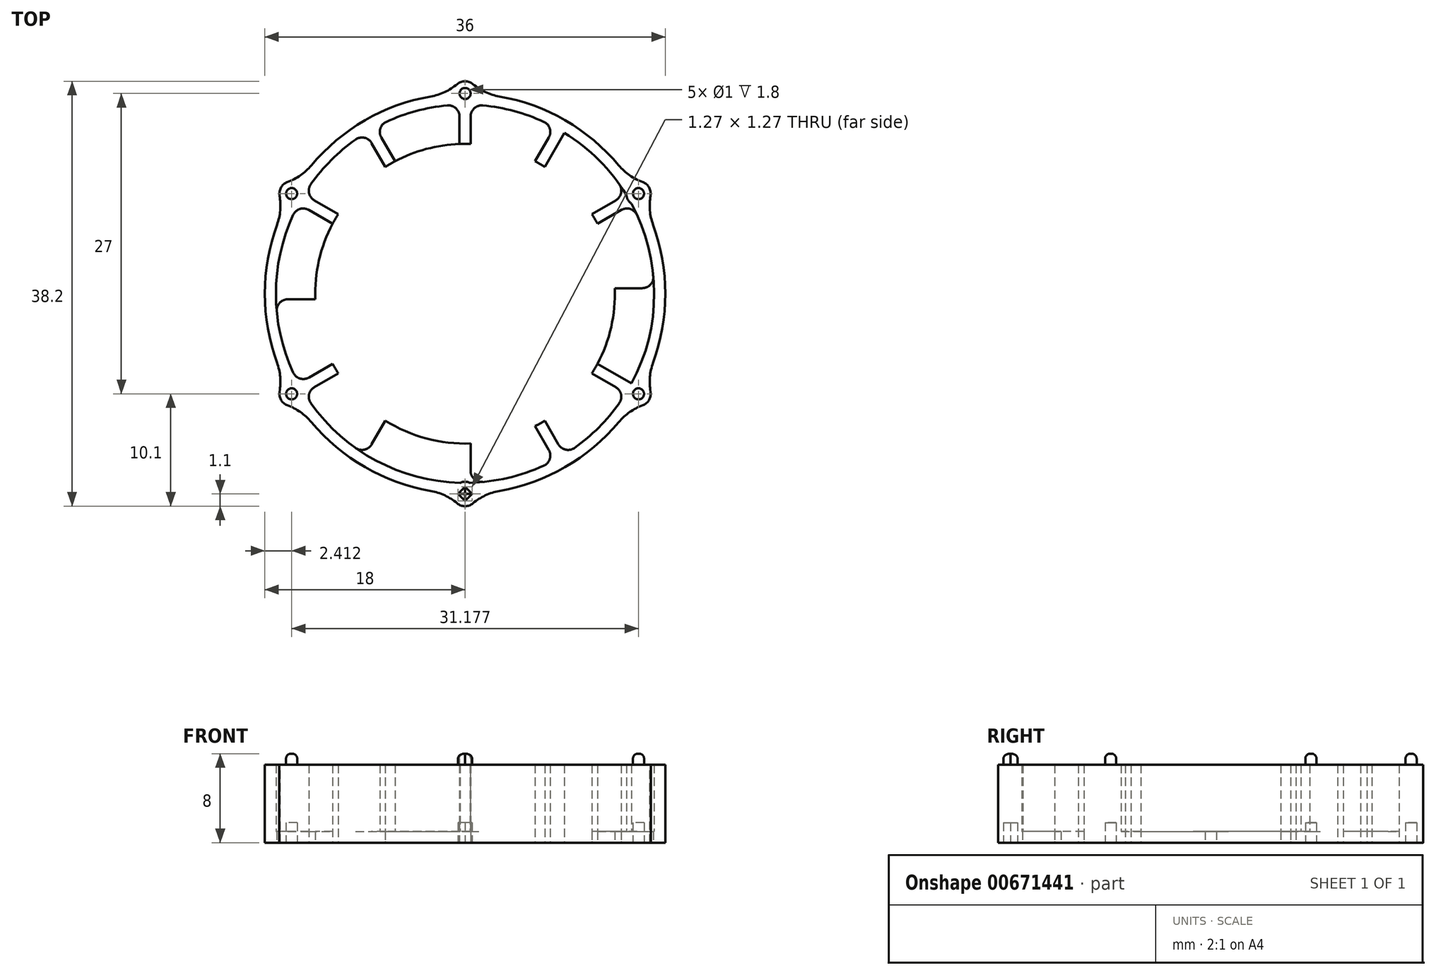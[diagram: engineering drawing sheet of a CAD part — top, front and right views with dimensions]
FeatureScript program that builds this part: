
annotation { "Feature Type Name" : "Feature", "Feature Type Description" : "" }
export const myFeature = defineFeature(function(context is Context, id is Id, definition is map)
    precondition{}
    {
        {
            var Q0;
            Q0=qCreatedBy(makeId("Top.planeOp"),FACE);
            var sketch = newSketch(context, id + "F0", { "sketchPlane" : qUnion([Q0])});
            skCircle(sketch, "E0", {"center": v(0, 0) * mm, "radius": 18 * mm});
            skCircle(sketch, "E1.0", {"center": v(0, 0) * mm, "radius": 17 * mm});
            skLineSegment(sketch, "E2.bottom", {"start": v(8.56, 15.83) * mm, "end": v(9.43, 15.33) * mm});
            skLineSegment(sketch, "E2.top", {"start": v(-9.43, -15.33) * mm, "end": v(-8.56, -15.83) * mm});
            skLineSegment(sketch, "E2.left", {"start": v(8.56, 15.83) * mm, "end": v(-9.43, -15.33) * mm});
            skLineSegment(sketch, "E2.right", {"start": v(9.43, 15.33) * mm, "end": v(-8.56, -15.83) * mm});
            skLineSegment(sketch, "E3.bottom", {"start": v(15.33, 9.43) * mm, "end": v(15.83, 8.56) * mm});
            skLineSegment(sketch, "E3.top", {"start": v(-15.83, -8.56) * mm, "end": v(-15.33, -9.43) * mm});
            skLineSegment(sketch, "E3.left", {"start": v(15.33, 9.43) * mm, "end": v(-15.83, -8.56) * mm});
            skLineSegment(sketch, "E3.right", {"start": v(15.83, 8.56) * mm, "end": v(-15.33, -9.43) * mm});
            skLineSegment(sketch, "E4", {"start": v(-38.35, 0) * mm, "end": v(39.17, 0) * mm, "construction": true});
            skLineSegment(sketch, "E5", {"start": v(0, 42.5) * mm, "end": v(0, -42.47) * mm, "construction": true});
            skLineSegment(sketch, "E6.bottom", {"start": v(-18, 0.5) * mm, "end": v(18, 0.5) * mm});
            skLineSegment(sketch, "E6.top", {"start": v(-18, -0.5) * mm, "end": v(18, -0.5) * mm});
            skLineSegment(sketch, "E6.left", {"start": v(-18, 0.5) * mm, "end": v(-18, -0.5) * mm});
            skLineSegment(sketch, "E6.right", {"start": v(18, 0.5) * mm, "end": v(18, -0.5) * mm});
            skLineSegment(sketch, "E7.bottom", {"start": v(-15.33, 9.43) * mm, "end": v(15.83, -8.56) * mm});
            skLineSegment(sketch, "E7.top", {"start": v(-15.83, 8.56) * mm, "end": v(15.33, -9.43) * mm});
            skLineSegment(sketch, "E7.left", {"start": v(-15.33, 9.43) * mm, "end": v(-15.83, 8.56) * mm});
            skLineSegment(sketch, "E7.right", {"start": v(15.83, -8.56) * mm, "end": v(15.33, -9.43) * mm});
            skLineSegment(sketch, "E8.bottom", {"start": v(-0.5, 18) * mm, "end": v(0.5, 18) * mm});
            skLineSegment(sketch, "E8.top", {"start": v(-0.5, -18) * mm, "end": v(0.5, -18) * mm});
            skLineSegment(sketch, "E8.left", {"start": v(-0.5, 18) * mm, "end": v(-0.5, -18) * mm});
            skLineSegment(sketch, "E8.right", {"start": v(0.5, 18) * mm, "end": v(0.5, -18) * mm});
            skLineSegment(sketch, "E9.bottom", {"start": v(-9.43, 15.33) * mm, "end": v(-8.56, 15.83) * mm});
            skLineSegment(sketch, "E9.top", {"start": v(8.56, -15.83) * mm, "end": v(9.43, -15.33) * mm});
            skLineSegment(sketch, "E9.left", {"start": v(-9.43, 15.33) * mm, "end": v(8.56, -15.83) * mm});
            skLineSegment(sketch, "E9.right", {"start": v(-8.56, 15.83) * mm, "end": v(9.43, -15.33) * mm});
            skCircle(sketch, "E10", {"center": v(0, 0) * mm, "radius": 13.47 * mm});
            skSolve(sketch);
        }
        {
            var Q0;
            Q0=qCreatedBy(makeId("Top.planeOp"),FACE);
            var sketch = newSketch(context, id + "F1", { "sketchPlane" : qUnion([Q0])});
            skCircle(sketch, "E11", {"center": v(0, 0) * mm, "radius": 18 * mm});
            skCircle(sketch, "E12", {"center": v(0, 0) * mm, "radius": 17 * mm});
            skSolve(sketch);
        }
        {
            var Q0;
            Q0=makeQuery(id+"F1.imprint","IMPRINT",FACE,{"disambiguationData":[TD([[makeQuery(id+"F1.imprint","IMPRINT",EDGE,{"derivedFrom":sQuery(id+"F1.wireOp",EDGE,"E11")}),1.0]])]});
            extrude(context, id + "F2", {"entities" : qUnion([Q0]), "depth" : 7 * mm, "offsetDistance" : 25 * mm});
        }
        {
            var Q0;
            {var subQ0=sQuery(id+"F0.wireOp",EDGE,"E7.bottom");var subQ1=sQuery(id+"F0.wireOp",EDGE,"E1.0");var subQ2=makeQuery(id+"F0.imprint","INTERSECT",VERTEX,{"disambiguationData":[OD(0.0)],"derivedFrom":[subQ1,subQ0]});Q0=makeQuery(id+"F0.imprint","IMPRINT",FACE,{"disambiguationData":[TD([[makeQuery(id+"F0.imprint","IMPRINT",EDGE,{"disambiguationData":[TD([[subQ2,-1.0]])],"derivedFrom":subQ1}),1.0]])]});}
            var Q1;
            {var subQ0=sQuery(id+"F0.wireOp",EDGE,"E2.right");var subQ1=sQuery(id+"F0.wireOp",EDGE,"E1.0");var subQ2=makeQuery(id+"F0.imprint","INTERSECT",VERTEX,{"disambiguationData":[OD(0.0)],"derivedFrom":[subQ1,subQ0]});Q1=makeQuery(id+"F0.imprint","IMPRINT",FACE,{"disambiguationData":[TD([[makeQuery(id+"F0.imprint","IMPRINT",EDGE,{"disambiguationData":[TD([[subQ2,-1.0]])],"derivedFrom":subQ1}),1.0]])]});}
            var Q2;
            {var subQ0=sQuery(id+"F0.wireOp",EDGE,"E3.left");var subQ1=sQuery(id+"F0.wireOp",EDGE,"E1.0");var subQ2=makeQuery(id+"F0.imprint","INTERSECT",VERTEX,{"disambiguationData":[OD(1.0)],"derivedFrom":[subQ1,subQ0]});Q2=makeQuery(id+"F0.imprint","IMPRINT",FACE,{"disambiguationData":[TD([[makeQuery(id+"F0.imprint","IMPRINT",EDGE,{"disambiguationData":[TD([[subQ2,-1.0]])],"derivedFrom":subQ1}),1.0]])]});}
            var Q3;
            {var subQ0=sQuery(id+"F0.wireOp",EDGE,"E9.right");var subQ1=sQuery(id+"F0.wireOp",EDGE,"E1.0");var subQ2=makeQuery(id+"F0.imprint","INTERSECT",VERTEX,{"disambiguationData":[OD(0.0)],"derivedFrom":[subQ1,subQ0]});Q3=makeQuery(id+"F0.imprint","IMPRINT",FACE,{"disambiguationData":[TD([[makeQuery(id+"F0.imprint","IMPRINT",EDGE,{"disambiguationData":[TD([[subQ2,-1.0]])],"derivedFrom":subQ1}),1.0]])]});}
            var Q4;
            {var subQ0=sQuery(id+"F0.wireOp",EDGE,"E8.right");var subQ1=sQuery(id+"F0.wireOp",EDGE,"E1.0");var subQ2=makeQuery(id+"F0.imprint","INTERSECT",VERTEX,{"disambiguationData":[OD(0.0)],"derivedFrom":[subQ1,subQ0]});Q4=makeQuery(id+"F0.imprint","IMPRINT",FACE,{"disambiguationData":[TD([[makeQuery(id+"F0.imprint","IMPRINT",EDGE,{"disambiguationData":[TD([[subQ2,-1.0]])],"derivedFrom":subQ1}),1.0]])]});}
            var Q5;
            {var subQ0=sQuery(id+"F0.wireOp",EDGE,"E7.top");var subQ1=sQuery(id+"F0.wireOp",EDGE,"E1.0");var subQ2=makeQuery(id+"F0.imprint","INTERSECT",VERTEX,{"disambiguationData":[OD(1.0)],"derivedFrom":[subQ1,subQ0]});Q5=makeQuery(id+"F0.imprint","IMPRINT",FACE,{"disambiguationData":[TD([[makeQuery(id+"F0.imprint","IMPRINT",EDGE,{"disambiguationData":[TD([[subQ2,-1.0]])],"derivedFrom":subQ1}),1.0]])]});}
            var Q6;
            {var subQ0=sQuery(id+"F0.wireOp",EDGE,"E9.left");var subQ1=sQuery(id+"F0.wireOp",EDGE,"E1.0");var subQ2=makeQuery(id+"F0.imprint","INTERSECT",VERTEX,{"disambiguationData":[OD(1.0)],"derivedFrom":[subQ1,subQ0]});Q6=makeQuery(id+"F0.imprint","IMPRINT",FACE,{"disambiguationData":[TD([[makeQuery(id+"F0.imprint","IMPRINT",EDGE,{"disambiguationData":[TD([[subQ2,-1.0]])],"derivedFrom":subQ1}),1.0]])]});}
            extrude(context, id + "F3", {"entities" : qUnion([Q0, Q1, Q2, Q3, Q4, Q5, Q6]), "operationType" : NewBodyOperationType.ADD, "depth" : 7 * mm, "offsetDistance" : 25 * mm});
        }
        {
            var Q0;
            Q0=makeQuery(id+"F1.imprint","IMPRINT",FACE,{"disambiguationData":[TD([[makeQuery(id+"F1.imprint","IMPRINT",EDGE,{"derivedFrom":sQuery(id+"F1.wireOp",EDGE,"E11")}),1.0]])]});
            var Q1;
            Q1=makeQuery(id+"F1.imprint","IMPRINT",FACE,{"disambiguationData":[TD([[makeQuery(id+"F1.imprint","IMPRINT",EDGE,{"derivedFrom":sQuery(id+"F1.wireOp",EDGE,"E12")}),1.0]])]});
            extrude(context, id + "F4", {"entities" : qUnion([Q0, Q1]), "operationType" : NewBodyOperationType.ADD, "depth" : 1 * mm, "offsetDistance" : 25 * mm});
        }
        {
            var Q0;
            Q0=qCreatedBy(makeId("Top.planeOp"),FACE);
            var sketch = newSketch(context, id + "F5", { "sketchPlane" : qUnion([Q0])});
            skCircle(sketch, "E13", {"center": v(0, 0) * mm, "radius": 18 * mm});
            skLineSegment(sketch, "E14", {"start": v(0, 18) * mm, "end": v(0, -18) * mm, "construction": true});
            skLineSegment(sketch, "E15", {"start": v(15.59, 9) * mm, "end": v(0, 0) * mm, "construction": true});
            skLineSegment(sketch, "E16", {"start": v(9, 15.59) * mm, "end": v(0, 0) * mm, "construction": true});
            skLineSegment(sketch, "E17", {"start": v(0, 0) * mm, "end": v(18, 0) * mm, "construction": true});
            skLineSegment(sketch, "E18", {"start": v(0, 0) * mm, "end": v(15.59, -9) * mm, "construction": true});
            skLineSegment(sketch, "E19", {"start": v(0, 0) * mm, "end": v(9, -15.59) * mm, "construction": true});
            skLineSegment(sketch, "E20", {"start": v(0, 0) * mm, "end": v(-9, 15.59) * mm, "construction": true});
            skLineSegment(sketch, "E21", {"start": v(0, 0) * mm, "end": v(-15.59, 9) * mm, "construction": true});
            skLineSegment(sketch, "E22", {"start": v(0, 0) * mm, "end": v(-18, 0) * mm, "construction": true});
            skLineSegment(sketch, "E23", {"start": v(0, 0) * mm, "end": v(-15.59, -9) * mm, "construction": true});
            skLineSegment(sketch, "E24", {"start": v(0, 0) * mm, "end": v(-9, -15.59) * mm, "construction": true});
            skCircle(sketch, "E25", {"center": v(0, 18) * mm, "radius": 1.1 * mm});
            skCircle(sketch, "E26", {"center": v(15.59, 9) * mm, "radius": 1.1 * mm});
            skCircle(sketch, "E27", {"center": v(15.59, -9) * mm, "radius": 1.1 * mm});
            skCircle(sketch, "E28", {"center": v(0, -18) * mm, "radius": 1.1 * mm});
            skCircle(sketch, "E29", {"center": v(-15.59, -9) * mm, "radius": 1.1 * mm});
            skCircle(sketch, "E30", {"center": v(-15.59, 9) * mm, "radius": 1.1 * mm});
            skCircle(sketch, "E31", {"center": v(-15.59, 9) * mm, "radius": 0.5 * mm});
            skCircle(sketch, "E32", {"center": v(0, 18) * mm, "radius": 0.5 * mm});
            skCircle(sketch, "E33", {"center": v(15.59, 9) * mm, "radius": 0.5 * mm});
            skCircle(sketch, "E34", {"center": v(15.59, -9) * mm, "radius": 0.5 * mm});
            skCircle(sketch, "E35", {"center": v(-15.59, -9) * mm, "radius": 0.5 * mm});
            skLineSegment(sketch, "E36.bottom", {"start": v(0.64, -18) * mm, "end": v(0, -18.64) * mm});
            skLineSegment(sketch, "E36.top", {"start": v(0, -17.36) * mm, "end": v(-0.64, -18) * mm});
            skLineSegment(sketch, "E36.left", {"start": v(0.64, -18) * mm, "end": v(0, -17.36) * mm});
            skLineSegment(sketch, "E36.right", {"start": v(0, -18.64) * mm, "end": v(-0.64, -18) * mm});
            skSolve(sketch);
        }
        {
            var Q0;
            {var subQ0=sQuery(id+"F5.wireOp",EDGE,"E30");var subQ1=sQuery(id+"F5.wireOp",EDGE,"E13");var subQ2=makeQuery(id+"F5.imprint","INTERSECT",VERTEX,{"disambiguationData":[OD(0.0)],"derivedFrom":[subQ1,subQ0]});Q0=makeQuery(id+"F5.imprint","IMPRINT",FACE,{"disambiguationData":[TD([[makeQuery(id+"F5.imprint","IMPRINT",EDGE,{"disambiguationData":[TD([[subQ2,-1.0]])],"derivedFrom":subQ1}),1.0]])]});}
            var Q1;
            {var subQ0=sQuery(id+"F5.wireOp",EDGE,"E30");var subQ1=sQuery(id+"F5.wireOp",EDGE,"E13");var subQ2=makeQuery(id+"F5.imprint","INTERSECT",VERTEX,{"disambiguationData":[OD(0.0)],"derivedFrom":[subQ1,subQ0]});Q1=makeQuery(id+"F5.imprint","IMPRINT",FACE,{"disambiguationData":[TD([[makeQuery(id+"F5.imprint","IMPRINT",EDGE,{"disambiguationData":[TD([[subQ2,-1.0]])],"derivedFrom":subQ1}),-1.0]])]});}
            var Q2;
            {var subQ0=sQuery(id+"F5.wireOp",EDGE,"E25");var subQ1=sQuery(id+"F5.wireOp",EDGE,"E13");var subQ2=makeQuery(id+"F5.imprint","INTERSECT",VERTEX,{"disambiguationData":[OD(0.0)],"derivedFrom":[subQ1,subQ0]});Q2=makeQuery(id+"F5.imprint","IMPRINT",FACE,{"disambiguationData":[TD([[makeQuery(id+"F5.imprint","IMPRINT",EDGE,{"disambiguationData":[TD([[subQ2,-1.0]])],"derivedFrom":subQ1}),1.0]])]});}
            var Q3;
            {var subQ0=sQuery(id+"F5.wireOp",EDGE,"E25");var subQ1=sQuery(id+"F5.wireOp",EDGE,"E13");var subQ2=makeQuery(id+"F5.imprint","INTERSECT",VERTEX,{"disambiguationData":[OD(0.0)],"derivedFrom":[subQ1,subQ0]});Q3=makeQuery(id+"F5.imprint","IMPRINT",FACE,{"disambiguationData":[TD([[makeQuery(id+"F5.imprint","IMPRINT",EDGE,{"disambiguationData":[TD([[subQ2,-1.0]])],"derivedFrom":subQ1}),-1.0]])]});}
            var Q4;
            {var subQ0=sQuery(id+"F5.wireOp",EDGE,"E26");var subQ1=sQuery(id+"F5.wireOp",EDGE,"E13");var subQ2=makeQuery(id+"F5.imprint","INTERSECT",VERTEX,{"disambiguationData":[OD(0.0)],"derivedFrom":[subQ1,subQ0]});Q4=makeQuery(id+"F5.imprint","IMPRINT",FACE,{"disambiguationData":[TD([[makeQuery(id+"F5.imprint","IMPRINT",EDGE,{"disambiguationData":[TD([[subQ2,-1.0]])],"derivedFrom":subQ1}),-1.0]])]});}
            var Q5;
            {var subQ0=sQuery(id+"F5.wireOp",EDGE,"E26");var subQ1=sQuery(id+"F5.wireOp",EDGE,"E13");var subQ2=makeQuery(id+"F5.imprint","INTERSECT",VERTEX,{"disambiguationData":[OD(0.0)],"derivedFrom":[subQ1,subQ0]});Q5=makeQuery(id+"F5.imprint","IMPRINT",FACE,{"disambiguationData":[TD([[makeQuery(id+"F5.imprint","IMPRINT",EDGE,{"disambiguationData":[TD([[subQ2,-1.0]])],"derivedFrom":subQ1}),1.0]])]});}
            var Q6;
            {var subQ0=sQuery(id+"F5.wireOp",EDGE,"E29");var subQ1=sQuery(id+"F5.wireOp",EDGE,"E13");var subQ2=makeQuery(id+"F5.imprint","INTERSECT",VERTEX,{"disambiguationData":[OD(0.0)],"derivedFrom":[subQ1,subQ0]});Q6=makeQuery(id+"F5.imprint","IMPRINT",FACE,{"disambiguationData":[TD([[makeQuery(id+"F5.imprint","IMPRINT",EDGE,{"disambiguationData":[TD([[subQ2,-1.0]])],"derivedFrom":subQ1}),1.0]])]});}
            var Q7;
            {var subQ0=sQuery(id+"F5.wireOp",EDGE,"E29");var subQ1=sQuery(id+"F5.wireOp",EDGE,"E13");var subQ2=makeQuery(id+"F5.imprint","INTERSECT",VERTEX,{"disambiguationData":[OD(0.0)],"derivedFrom":[subQ1,subQ0]});Q7=makeQuery(id+"F5.imprint","IMPRINT",FACE,{"disambiguationData":[TD([[makeQuery(id+"F5.imprint","IMPRINT",EDGE,{"disambiguationData":[TD([[subQ2,-1.0]])],"derivedFrom":subQ1}),-1.0]])]});}
            var Q8;
            {var subQ3=sQuery(id+"F5.wireOp",EDGE,"E13");var subQ5=sQuery(id+"F5.wireOp",EDGE,"E28");var subQ6=makeQuery(id+"F5.imprint","INTERSECT",VERTEX,{"disambiguationData":[OD(0.0)],"derivedFrom":[subQ3,subQ5]});Q8=makeQuery(id+"F5.imprint","IMPRINT",FACE,{"disambiguationData":[TD([[makeQuery(id+"F5.imprint","IMPRINT",EDGE,{"disambiguationData":[TD([[subQ6,-1.0]])],"derivedFrom":subQ3}),1.0]])]});}
            var Q9;
            {var subQ6=sQuery(id+"F5.wireOp",EDGE,"E36.bottom");Q9=makeQuery(id+"F5.imprint","IMPRINT",FACE,{"disambiguationData":[TD([[makeQuery(id+"F5.imprint","IMPRINT",EDGE,{"derivedFrom":subQ6}),1.0]])]});}
            var Q10;
            {var subQ0=sQuery(id+"F5.wireOp",EDGE,"E27");var subQ1=sQuery(id+"F5.wireOp",EDGE,"E13");var subQ2=makeQuery(id+"F5.imprint","INTERSECT",VERTEX,{"disambiguationData":[OD(0.0)],"derivedFrom":[subQ1,subQ0]});Q10=makeQuery(id+"F5.imprint","IMPRINT",FACE,{"disambiguationData":[TD([[makeQuery(id+"F5.imprint","IMPRINT",EDGE,{"disambiguationData":[TD([[subQ2,-1.0]])],"derivedFrom":subQ1}),-1.0]])]});}
            var Q11;
            {var subQ0=sQuery(id+"F5.wireOp",EDGE,"E27");var subQ1=sQuery(id+"F5.wireOp",EDGE,"E13");var subQ2=makeQuery(id+"F5.imprint","INTERSECT",VERTEX,{"disambiguationData":[OD(0.0)],"derivedFrom":[subQ1,subQ0]});Q11=makeQuery(id+"F5.imprint","IMPRINT",FACE,{"disambiguationData":[TD([[makeQuery(id+"F5.imprint","IMPRINT",EDGE,{"disambiguationData":[TD([[subQ2,-1.0]])],"derivedFrom":subQ1}),1.0]])]});}
            var Q12;
            {var subQ0=sQuery(id+"F5.wireOp",EDGE,"E31");var subQ1=sQuery(id+"F5.wireOp",EDGE,"E13");var subQ2=makeQuery(id+"F5.imprint","INTERSECT",VERTEX,{"disambiguationData":[OD(0.0)],"derivedFrom":[subQ1,subQ0]});Q12=makeQuery(id+"F5.imprint","IMPRINT",FACE,{"disambiguationData":[TD([[makeQuery(id+"F5.imprint","IMPRINT",EDGE,{"disambiguationData":[TD([[subQ2,-1.0]])],"derivedFrom":subQ1}),1.0]])]});}
            var Q13;
            {var subQ0=sQuery(id+"F5.wireOp",EDGE,"E31");var subQ1=sQuery(id+"F5.wireOp",EDGE,"E13");var subQ2=makeQuery(id+"F5.imprint","INTERSECT",VERTEX,{"disambiguationData":[OD(0.0)],"derivedFrom":[subQ1,subQ0]});Q13=makeQuery(id+"F5.imprint","IMPRINT",FACE,{"disambiguationData":[TD([[makeQuery(id+"F5.imprint","IMPRINT",EDGE,{"disambiguationData":[TD([[subQ2,-1.0]])],"derivedFrom":subQ1}),-1.0]])]});}
            var Q14;
            {var subQ0=sQuery(id+"F5.wireOp",EDGE,"E32");var subQ1=sQuery(id+"F5.wireOp",EDGE,"E13");var subQ2=makeQuery(id+"F5.imprint","INTERSECT",VERTEX,{"disambiguationData":[OD(0.0)],"derivedFrom":[subQ1,subQ0]});Q14=makeQuery(id+"F5.imprint","IMPRINT",FACE,{"disambiguationData":[TD([[makeQuery(id+"F5.imprint","IMPRINT",EDGE,{"disambiguationData":[TD([[subQ2,-1.0]])],"derivedFrom":subQ1}),-1.0]])]});}
            var Q15;
            {var subQ0=sQuery(id+"F5.wireOp",EDGE,"E32");var subQ1=sQuery(id+"F5.wireOp",EDGE,"E13");var subQ2=makeQuery(id+"F5.imprint","INTERSECT",VERTEX,{"disambiguationData":[OD(0.0)],"derivedFrom":[subQ1,subQ0]});Q15=makeQuery(id+"F5.imprint","IMPRINT",FACE,{"disambiguationData":[TD([[makeQuery(id+"F5.imprint","IMPRINT",EDGE,{"disambiguationData":[TD([[subQ2,-1.0]])],"derivedFrom":subQ1}),1.0]])]});}
            var Q16;
            {var subQ0=sQuery(id+"F5.wireOp",EDGE,"E33");var subQ1=sQuery(id+"F5.wireOp",EDGE,"E13");var subQ2=makeQuery(id+"F5.imprint","INTERSECT",VERTEX,{"disambiguationData":[OD(0.0)],"derivedFrom":[subQ1,subQ0]});Q16=makeQuery(id+"F5.imprint","IMPRINT",FACE,{"disambiguationData":[TD([[makeQuery(id+"F5.imprint","IMPRINT",EDGE,{"disambiguationData":[TD([[subQ2,-1.0]])],"derivedFrom":subQ1}),-1.0]])]});}
            var Q17;
            {var subQ0=sQuery(id+"F5.wireOp",EDGE,"E33");var subQ1=sQuery(id+"F5.wireOp",EDGE,"E13");var subQ2=makeQuery(id+"F5.imprint","INTERSECT",VERTEX,{"disambiguationData":[OD(0.0)],"derivedFrom":[subQ1,subQ0]});Q17=makeQuery(id+"F5.imprint","IMPRINT",FACE,{"disambiguationData":[TD([[makeQuery(id+"F5.imprint","IMPRINT",EDGE,{"disambiguationData":[TD([[subQ2,-1.0]])],"derivedFrom":subQ1}),1.0]])]});}
            var Q18;
            {var subQ0=sQuery(id+"F5.wireOp",EDGE,"E34");var subQ1=sQuery(id+"F5.wireOp",EDGE,"E13");var subQ2=makeQuery(id+"F5.imprint","INTERSECT",VERTEX,{"disambiguationData":[OD(0.0)],"derivedFrom":[subQ1,subQ0]});Q18=makeQuery(id+"F5.imprint","IMPRINT",FACE,{"disambiguationData":[TD([[makeQuery(id+"F5.imprint","IMPRINT",EDGE,{"disambiguationData":[TD([[subQ2,-1.0]])],"derivedFrom":subQ1}),-1.0]])]});}
            var Q19;
            {var subQ0=sQuery(id+"F5.wireOp",EDGE,"E34");var subQ1=sQuery(id+"F5.wireOp",EDGE,"E13");var subQ2=makeQuery(id+"F5.imprint","INTERSECT",VERTEX,{"disambiguationData":[OD(0.0)],"derivedFrom":[subQ1,subQ0]});Q19=makeQuery(id+"F5.imprint","IMPRINT",FACE,{"disambiguationData":[TD([[makeQuery(id+"F5.imprint","IMPRINT",EDGE,{"disambiguationData":[TD([[subQ2,-1.0]])],"derivedFrom":subQ1}),1.0]])]});}
            var Q20;
            {var subQ1=sQuery(id+"F5.wireOp",EDGE,"E36.bottom");Q20=makeQuery(id+"F5.imprint","IMPRINT",FACE,{"disambiguationData":[TD([[makeQuery(id+"F5.imprint","IMPRINT",EDGE,{"derivedFrom":subQ1}),-1.0]])]});}
            var Q21;
            {var subQ0=sQuery(id+"F5.wireOp",EDGE,"E35");var subQ1=sQuery(id+"F5.wireOp",EDGE,"E13");var subQ2=makeQuery(id+"F5.imprint","INTERSECT",VERTEX,{"disambiguationData":[OD(0.0)],"derivedFrom":[subQ1,subQ0]});Q21=makeQuery(id+"F5.imprint","IMPRINT",FACE,{"disambiguationData":[TD([[makeQuery(id+"F5.imprint","IMPRINT",EDGE,{"disambiguationData":[TD([[subQ2,-1.0]])],"derivedFrom":subQ1}),-1.0]])]});}
            var Q22;
            {var subQ0=sQuery(id+"F5.wireOp",EDGE,"E35");var subQ1=sQuery(id+"F5.wireOp",EDGE,"E13");var subQ2=makeQuery(id+"F5.imprint","INTERSECT",VERTEX,{"disambiguationData":[OD(0.0)],"derivedFrom":[subQ1,subQ0]});Q22=makeQuery(id+"F5.imprint","IMPRINT",FACE,{"disambiguationData":[TD([[makeQuery(id+"F5.imprint","IMPRINT",EDGE,{"disambiguationData":[TD([[subQ2,-1.0]])],"derivedFrom":subQ1}),1.0]])]});}
            var Q23;
            {var subQ0=sQuery(id+"F5.wireOp",EDGE,"E36.top");var subQ1=sQuery(id+"F5.wireOp",EDGE,"E13");var subQ2=makeQuery(id+"F5.imprint","INTERSECT",VERTEX,{"derivedFrom":[subQ1,subQ0]});Q23=makeQuery(id+"F5.imprint","IMPRINT",FACE,{"disambiguationData":[TD([[makeQuery(id+"F5.imprint","IMPRINT",EDGE,{"disambiguationData":[TD([[subQ2,-1.0]])],"derivedFrom":subQ1}),1.0]])]});}
            extrude(context, id + "F6", {"entities" : qUnion([Q0, Q1, Q2, Q3, Q4, Q5, Q6, Q7, Q8, Q9, Q10, Q11, Q12, Q13, Q14, Q15, Q16, Q17, Q18, Q19, Q20, Q21, Q22, Q23]), "operationType" : NewBodyOperationType.ADD, "depth" : 7 * mm, "offsetDistance" : 25 * mm});
        }
        {
            var Q0;
            {var subQ0=sQuery(id+"F0.wireOp",EDGE,"E8.right");var subQ1=sQuery(id+"F0.wireOp",EDGE,"E1.0");Q0=makeQuery(id+"F3.opExtrude","SWEPT_EDGE",EDGE,{"disambiguationData":[OSD([subQ1,subQ0]),TDD([makeQuery(id+"F0.imprint","INTERSECT",VERTEX,{"disambiguationData":[OD(1.0)],"derivedFrom":[subQ1,subQ0]})])]});}
            var Q1;
            {var subQ0=sQuery(id+"F0.wireOp",EDGE,"E2.left");var subQ1=sQuery(id+"F0.wireOp",EDGE,"E1.0");Q1=makeQuery(id+"F3.opExtrude","SWEPT_EDGE",EDGE,{"disambiguationData":[OSD([subQ1,subQ0]),TDD([makeQuery(id+"F0.imprint","INTERSECT",VERTEX,{"disambiguationData":[OD(1.0)],"derivedFrom":[subQ1,subQ0]})])]});}
            var Q2;
            {var subQ0=sQuery(id+"F0.wireOp",EDGE,"E3.left");var subQ1=sQuery(id+"F0.wireOp",EDGE,"E1.0");Q2=makeQuery(id+"F3.opExtrude","SWEPT_EDGE",EDGE,{"disambiguationData":[OSD([subQ1,subQ0]),TDD([makeQuery(id+"F0.imprint","INTERSECT",VERTEX,{"disambiguationData":[OD(1.0)],"derivedFrom":[subQ1,subQ0]})])]});}
            var Q3;
            {var subQ0=sQuery(id+"F0.wireOp",EDGE,"E6.bottom");var subQ1=sQuery(id+"F0.wireOp",EDGE,"E1.0");Q3=makeQuery(id+"F3.opExtrude","SWEPT_EDGE",EDGE,{"disambiguationData":[OSD([subQ1,subQ0]),TDD([makeQuery(id+"F0.imprint","INTERSECT",VERTEX,{"disambiguationData":[OD(1.0)],"derivedFrom":[subQ1,subQ0]})])]});}
            var Q4;
            {var subQ0=sQuery(id+"F0.wireOp",EDGE,"E9.right");var subQ1=sQuery(id+"F0.wireOp",EDGE,"E1.0");Q4=makeQuery(id+"F3.opExtrude","SWEPT_EDGE",EDGE,{"disambiguationData":[OSD([subQ1,subQ0]),TDD([makeQuery(id+"F0.imprint","INTERSECT",VERTEX,{"disambiguationData":[OD(1.0)],"derivedFrom":[subQ1,subQ0]})])]});}
            var Q5;
            {var subQ0=sQuery(id+"F0.wireOp",EDGE,"E7.bottom");var subQ1=sQuery(id+"F0.wireOp",EDGE,"E1.0");Q5=makeQuery(id+"F3.opExtrude","SWEPT_EDGE",EDGE,{"disambiguationData":[OSD([subQ1,subQ0]),TDD([makeQuery(id+"F0.imprint","INTERSECT",VERTEX,{"disambiguationData":[OD(1.0)],"derivedFrom":[subQ1,subQ0]})])]});}
            var Q6;
            {var subQ0=sQuery(id+"F0.wireOp",EDGE,"E8.left");var subQ1=sQuery(id+"F0.wireOp",EDGE,"E1.0");Q6=makeQuery(id+"F3.opExtrude","SWEPT_EDGE",EDGE,{"disambiguationData":[OSD([subQ1,subQ0]),TDD([makeQuery(id+"F0.imprint","INTERSECT",VERTEX,{"disambiguationData":[OD(0.0)],"derivedFrom":[subQ1,subQ0]})])]});}
            var Q7;
            {var subQ0=sQuery(id+"F0.wireOp",EDGE,"E2.left");var subQ1=sQuery(id+"F0.wireOp",EDGE,"E1.0");Q7=makeQuery(id+"F3.opExtrude","SWEPT_EDGE",EDGE,{"disambiguationData":[OSD([subQ1,subQ0]),TDD([makeQuery(id+"F0.imprint","INTERSECT",VERTEX,{"disambiguationData":[OD(0.0)],"derivedFrom":[subQ1,subQ0]})])]});}
            var Q8;
            {var subQ0=sQuery(id+"F0.wireOp",EDGE,"E3.left");var subQ1=sQuery(id+"F0.wireOp",EDGE,"E1.0");Q8=makeQuery(id+"F3.opExtrude","SWEPT_EDGE",EDGE,{"disambiguationData":[OSD([subQ1,subQ0]),TDD([makeQuery(id+"F0.imprint","INTERSECT",VERTEX,{"disambiguationData":[OD(0.0)],"derivedFrom":[subQ1,subQ0]})])]});}
            var Q9;
            {var subQ0=sQuery(id+"F0.wireOp",EDGE,"E6.top");var subQ1=sQuery(id+"F0.wireOp",EDGE,"E1.0");Q9=makeQuery(id+"F3.opExtrude","SWEPT_EDGE",EDGE,{"disambiguationData":[OSD([subQ1,subQ0]),TDD([makeQuery(id+"F0.imprint","INTERSECT",VERTEX,{"disambiguationData":[OD(1.0)],"derivedFrom":[subQ1,subQ0]})])]});}
            var Q10;
            {var subQ0=sQuery(id+"F0.wireOp",EDGE,"E7.top");var subQ1=sQuery(id+"F0.wireOp",EDGE,"E1.0");Q10=makeQuery(id+"F3.opExtrude","SWEPT_EDGE",EDGE,{"disambiguationData":[OSD([subQ1,subQ0]),TDD([makeQuery(id+"F0.imprint","INTERSECT",VERTEX,{"disambiguationData":[OD(0.0)],"derivedFrom":[subQ1,subQ0]})])]});}
            var Q11;
            {var subQ0=sQuery(id+"F0.wireOp",EDGE,"E6.top");var subQ1=sQuery(id+"F0.wireOp",EDGE,"E1.0");Q11=makeQuery(id+"F3.opExtrude","SWEPT_EDGE",EDGE,{"disambiguationData":[OSD([subQ1,subQ0]),TDD([makeQuery(id+"F0.imprint","INTERSECT",VERTEX,{"disambiguationData":[OD(0.0)],"derivedFrom":[subQ1,subQ0]})])]});}
            var Q12;
            {var subQ0=sQuery(id+"F0.wireOp",EDGE,"E9.left");var subQ1=sQuery(id+"F0.wireOp",EDGE,"E1.0");Q12=makeQuery(id+"F3.opExtrude","SWEPT_EDGE",EDGE,{"disambiguationData":[OSD([subQ1,subQ0]),TDD([makeQuery(id+"F0.imprint","INTERSECT",VERTEX,{"disambiguationData":[OD(0.0)],"derivedFrom":[subQ1,subQ0]})])]});}
            var Q13;
            {var subQ0=sQuery(id+"F0.wireOp",EDGE,"E8.right");var subQ1=sQuery(id+"F0.wireOp",EDGE,"E1.0");Q13=makeQuery(id+"F3.opExtrude","SWEPT_EDGE",EDGE,{"disambiguationData":[OSD([subQ1,subQ0]),TDD([makeQuery(id+"F0.imprint","INTERSECT",VERTEX,{"disambiguationData":[OD(0.0)],"derivedFrom":[subQ1,subQ0]})])]});}
            var Q14;
            {var subQ0=sQuery(id+"F0.wireOp",EDGE,"E7.bottom");var subQ1=sQuery(id+"F0.wireOp",EDGE,"E1.0");Q14=makeQuery(id+"F3.opExtrude","SWEPT_EDGE",EDGE,{"disambiguationData":[OSD([subQ1,subQ0]),TDD([makeQuery(id+"F0.imprint","INTERSECT",VERTEX,{"disambiguationData":[OD(0.0)],"derivedFrom":[subQ1,subQ0]})])]});}
            var Q15;
            {var subQ0=sQuery(id+"F0.wireOp",EDGE,"E9.right");var subQ1=sQuery(id+"F0.wireOp",EDGE,"E1.0");Q15=makeQuery(id+"F3.opExtrude","SWEPT_EDGE",EDGE,{"disambiguationData":[OSD([subQ1,subQ0]),TDD([makeQuery(id+"F0.imprint","INTERSECT",VERTEX,{"disambiguationData":[OD(0.0)],"derivedFrom":[subQ1,subQ0]})])]});}
            var Q16;
            {var subQ0=sQuery(id+"F0.wireOp",EDGE,"E3.right");var subQ1=sQuery(id+"F0.wireOp",EDGE,"E1.0");Q16=makeQuery(id+"F3.opExtrude","SWEPT_EDGE",EDGE,{"disambiguationData":[OSD([subQ1,subQ0]),TDD([makeQuery(id+"F0.imprint","INTERSECT",VERTEX,{"disambiguationData":[OD(1.0)],"derivedFrom":[subQ1,subQ0]})])]});}
            var Q17;
            {var subQ0=sQuery(id+"F0.wireOp",EDGE,"E2.right");var subQ1=sQuery(id+"F0.wireOp",EDGE,"E1.0");Q17=makeQuery(id+"F3.opExtrude","SWEPT_EDGE",EDGE,{"disambiguationData":[OSD([subQ1,subQ0]),TDD([makeQuery(id+"F0.imprint","INTERSECT",VERTEX,{"disambiguationData":[OD(1.0)],"derivedFrom":[subQ1,subQ0]})])]});}
            var Q18;
            {var subQ0=sQuery(id+"F0.wireOp",EDGE,"E3.right");var subQ1=sQuery(id+"F0.wireOp",EDGE,"E1.0");Q18=makeQuery(id+"F3.opExtrude","SWEPT_EDGE",EDGE,{"disambiguationData":[OSD([subQ1,subQ0]),TDD([makeQuery(id+"F0.imprint","INTERSECT",VERTEX,{"disambiguationData":[OD(0.0)],"derivedFrom":[subQ1,subQ0]})])]});}
            var Q19;
            {var subQ0=sQuery(id+"F0.wireOp",EDGE,"E2.right");var subQ1=sQuery(id+"F0.wireOp",EDGE,"E1.0");Q19=makeQuery(id+"F3.opExtrude","SWEPT_EDGE",EDGE,{"disambiguationData":[OSD([subQ1,subQ0]),TDD([makeQuery(id+"F0.imprint","INTERSECT",VERTEX,{"disambiguationData":[OD(0.0)],"derivedFrom":[subQ1,subQ0]})])]});}
            var Q20;
            {var subQ0=sQuery(id+"F0.wireOp",EDGE,"E8.left");var subQ1=sQuery(id+"F0.wireOp",EDGE,"E1.0");Q20=makeQuery(id+"F3.opExtrude","SWEPT_EDGE",EDGE,{"disambiguationData":[OSD([subQ1,subQ0]),TDD([makeQuery(id+"F0.imprint","INTERSECT",VERTEX,{"disambiguationData":[OD(1.0)],"derivedFrom":[subQ1,subQ0]})])]});}
            var Q21;
            {var subQ0=sQuery(id+"F0.wireOp",EDGE,"E9.left");var subQ1=sQuery(id+"F0.wireOp",EDGE,"E1.0");Q21=makeQuery(id+"F3.opExtrude","SWEPT_EDGE",EDGE,{"disambiguationData":[OSD([subQ1,subQ0]),TDD([makeQuery(id+"F0.imprint","INTERSECT",VERTEX,{"disambiguationData":[OD(1.0)],"derivedFrom":[subQ1,subQ0]})])]});}
            var Q22;
            {var subQ0=sQuery(id+"F0.wireOp",EDGE,"E7.top");var subQ1=sQuery(id+"F0.wireOp",EDGE,"E1.0");Q22=makeQuery(id+"F3.opExtrude","SWEPT_EDGE",EDGE,{"disambiguationData":[OSD([subQ1,subQ0]),TDD([makeQuery(id+"F0.imprint","INTERSECT",VERTEX,{"disambiguationData":[OD(1.0)],"derivedFrom":[subQ1,subQ0]})])]});}
            var Q23;
            {var subQ0=sQuery(id+"F0.wireOp",EDGE,"E6.bottom");var subQ1=sQuery(id+"F0.wireOp",EDGE,"E1.0");Q23=makeQuery(id+"F3.opExtrude","SWEPT_EDGE",EDGE,{"disambiguationData":[OSD([subQ1,subQ0]),TDD([makeQuery(id+"F0.imprint","INTERSECT",VERTEX,{"disambiguationData":[OD(0.0)],"derivedFrom":[subQ1,subQ0]})])]});}
            fillet(context, id + "F7", {"entities" : qUnion([Q0, Q1, Q2, Q3, Q4, Q5, Q6, Q7, Q8, Q9, Q10, Q11, Q12, Q13, Q14, Q15, Q16, Q17, Q18, Q19, Q20, Q21, Q22, Q23]), "radius" : 1 * mm, "tangentPropagation" : true, "allowEdgeOverflow" : false});
        }
        {
            var Q0;
            Q0=makeQuery(id+"F6.boolean.opBoolean","INTERSECT",EDGE,{"disambiguationData":[OD(0.0)],"derivedFrom":[makeQuery(id+"F2.opExtrude","SWEPT_FACE",FACE,{"disambiguationData":[OSD([sQuery(id+"F1.wireOp",EDGE,"E11")])]}),makeQuery(id+"F6.opExtrude","SWEPT_FACE",FACE,{"disambiguationData":[OSD([sQuery(id+"F5.wireOp",EDGE,"E30")])]})]});
            var Q1;
            Q1=makeQuery(id+"F6.boolean.opBoolean","INTERSECT",EDGE,{"disambiguationData":[OD(1.0)],"derivedFrom":[makeQuery(id+"F2.opExtrude","SWEPT_FACE",FACE,{"disambiguationData":[OSD([sQuery(id+"F1.wireOp",EDGE,"E11")])]}),makeQuery(id+"F6.opExtrude","SWEPT_FACE",FACE,{"disambiguationData":[OSD([sQuery(id+"F5.wireOp",EDGE,"E30")])]})]});
            var Q2;
            Q2=makeQuery(id+"F6.boolean.opBoolean","INTERSECT",EDGE,{"disambiguationData":[OD(1.0)],"derivedFrom":[makeQuery(id+"F2.opExtrude","SWEPT_FACE",FACE,{"disambiguationData":[OSD([sQuery(id+"F1.wireOp",EDGE,"E11")])]}),makeQuery(id+"F6.opExtrude","SWEPT_FACE",FACE,{"disambiguationData":[OSD([sQuery(id+"F5.wireOp",EDGE,"E25")])]})]});
            var Q3;
            Q3=makeQuery(id+"F6.boolean.opBoolean","INTERSECT",EDGE,{"disambiguationData":[OD(1.0)],"derivedFrom":[makeQuery(id+"F2.opExtrude","SWEPT_FACE",FACE,{"disambiguationData":[OSD([sQuery(id+"F1.wireOp",EDGE,"E11")])]}),makeQuery(id+"F6.opExtrude","SWEPT_FACE",FACE,{"disambiguationData":[OSD([sQuery(id+"F5.wireOp",EDGE,"E29")])]})]});
            var Q4;
            Q4=makeQuery(id+"F6.boolean.opBoolean","INTERSECT",EDGE,{"disambiguationData":[OD(0.0)],"derivedFrom":[makeQuery(id+"F2.opExtrude","SWEPT_FACE",FACE,{"disambiguationData":[OSD([sQuery(id+"F1.wireOp",EDGE,"E11")])]}),makeQuery(id+"F6.opExtrude","SWEPT_FACE",FACE,{"disambiguationData":[OSD([sQuery(id+"F5.wireOp",EDGE,"E29")])]})]});
            var Q5;
            Q5=makeQuery(id+"F6.boolean.opBoolean","INTERSECT",EDGE,{"disambiguationData":[OD(1.0)],"derivedFrom":[makeQuery(id+"F2.opExtrude","SWEPT_FACE",FACE,{"disambiguationData":[OSD([sQuery(id+"F1.wireOp",EDGE,"E11")])]}),makeQuery(id+"F6.opExtrude","SWEPT_FACE",FACE,{"disambiguationData":[OSD([sQuery(id+"F5.wireOp",EDGE,"E28")])]})]});
            var Q6;
            Q6=makeQuery(id+"F6.boolean.opBoolean","INTERSECT",EDGE,{"disambiguationData":[OD(0.0)],"derivedFrom":[makeQuery(id+"F2.opExtrude","SWEPT_FACE",FACE,{"disambiguationData":[OSD([sQuery(id+"F1.wireOp",EDGE,"E11")])]}),makeQuery(id+"F6.opExtrude","SWEPT_FACE",FACE,{"disambiguationData":[OSD([sQuery(id+"F5.wireOp",EDGE,"E28")])]})]});
            var Q7;
            Q7=makeQuery(id+"F6.boolean.opBoolean","INTERSECT",EDGE,{"disambiguationData":[OD(1.0)],"derivedFrom":[makeQuery(id+"F2.opExtrude","SWEPT_FACE",FACE,{"disambiguationData":[OSD([sQuery(id+"F1.wireOp",EDGE,"E11")])]}),makeQuery(id+"F6.opExtrude","SWEPT_FACE",FACE,{"disambiguationData":[OSD([sQuery(id+"F5.wireOp",EDGE,"E27")])]})]});
            var Q8;
            Q8=makeQuery(id+"F6.boolean.opBoolean","INTERSECT",EDGE,{"disambiguationData":[OD(0.0)],"derivedFrom":[makeQuery(id+"F2.opExtrude","SWEPT_FACE",FACE,{"disambiguationData":[OSD([sQuery(id+"F1.wireOp",EDGE,"E11")])]}),makeQuery(id+"F6.opExtrude","SWEPT_FACE",FACE,{"disambiguationData":[OSD([sQuery(id+"F5.wireOp",EDGE,"E27")])]})]});
            var Q9;
            Q9=makeQuery(id+"F6.boolean.opBoolean","INTERSECT",EDGE,{"disambiguationData":[OD(1.0)],"derivedFrom":[makeQuery(id+"F2.opExtrude","SWEPT_FACE",FACE,{"disambiguationData":[OSD([sQuery(id+"F1.wireOp",EDGE,"E11")])]}),makeQuery(id+"F6.opExtrude","SWEPT_FACE",FACE,{"disambiguationData":[OSD([sQuery(id+"F5.wireOp",EDGE,"E26")])]})]});
            var Q10;
            Q10=makeQuery(id+"F6.boolean.opBoolean","INTERSECT",EDGE,{"disambiguationData":[OD(0.0)],"derivedFrom":[makeQuery(id+"F2.opExtrude","SWEPT_FACE",FACE,{"disambiguationData":[OSD([sQuery(id+"F1.wireOp",EDGE,"E11")])]}),makeQuery(id+"F6.opExtrude","SWEPT_FACE",FACE,{"disambiguationData":[OSD([sQuery(id+"F5.wireOp",EDGE,"E26")])]})]});
            var Q11;
            Q11=makeQuery(id+"F6.boolean.opBoolean","INTERSECT",EDGE,{"disambiguationData":[OD(0.0)],"derivedFrom":[makeQuery(id+"F2.opExtrude","SWEPT_FACE",FACE,{"disambiguationData":[OSD([sQuery(id+"F1.wireOp",EDGE,"E11")])]}),makeQuery(id+"F6.opExtrude","SWEPT_FACE",FACE,{"disambiguationData":[OSD([sQuery(id+"F5.wireOp",EDGE,"E25")])]})]});
            fillet(context, id + "F8", {"entities" : qUnion([Q0, Q1, Q2, Q3, Q4, Q5, Q6, Q7, Q8, Q9, Q10, Q11]), "radius" : 5 * mm, "tangentPropagation" : true, "allowEdgeOverflow" : false});
        }
        {
            var Q0;
            {var subQ0=sQuery(id+"F5.wireOp",EDGE,"E31");var subQ1=sQuery(id+"F5.wireOp",EDGE,"E13");var subQ2=makeQuery(id+"F5.imprint","INTERSECT",VERTEX,{"disambiguationData":[OD(0.0)],"derivedFrom":[subQ1,subQ0]});Q0=makeQuery(id+"F5.imprint","IMPRINT",FACE,{"disambiguationData":[TD([[makeQuery(id+"F5.imprint","IMPRINT",EDGE,{"disambiguationData":[TD([[subQ2,-1.0]])],"derivedFrom":subQ1}),-1.0]])]});}
            var Q1;
            {var subQ0=sQuery(id+"F5.wireOp",EDGE,"E31");var subQ1=sQuery(id+"F5.wireOp",EDGE,"E13");var subQ2=makeQuery(id+"F5.imprint","INTERSECT",VERTEX,{"disambiguationData":[OD(0.0)],"derivedFrom":[subQ1,subQ0]});Q1=makeQuery(id+"F5.imprint","IMPRINT",FACE,{"disambiguationData":[TD([[makeQuery(id+"F5.imprint","IMPRINT",EDGE,{"disambiguationData":[TD([[subQ2,-1.0]])],"derivedFrom":subQ1}),1.0]])]});}
            var Q2;
            {var subQ0=sQuery(id+"F5.wireOp",EDGE,"E32");var subQ1=sQuery(id+"F5.wireOp",EDGE,"E13");var subQ2=makeQuery(id+"F5.imprint","INTERSECT",VERTEX,{"disambiguationData":[OD(0.0)],"derivedFrom":[subQ1,subQ0]});Q2=makeQuery(id+"F5.imprint","IMPRINT",FACE,{"disambiguationData":[TD([[makeQuery(id+"F5.imprint","IMPRINT",EDGE,{"disambiguationData":[TD([[subQ2,-1.0]])],"derivedFrom":subQ1}),-1.0]])]});}
            var Q3;
            {var subQ0=sQuery(id+"F5.wireOp",EDGE,"E32");var subQ1=sQuery(id+"F5.wireOp",EDGE,"E13");var subQ2=makeQuery(id+"F5.imprint","INTERSECT",VERTEX,{"disambiguationData":[OD(0.0)],"derivedFrom":[subQ1,subQ0]});Q3=makeQuery(id+"F5.imprint","IMPRINT",FACE,{"disambiguationData":[TD([[makeQuery(id+"F5.imprint","IMPRINT",EDGE,{"disambiguationData":[TD([[subQ2,-1.0]])],"derivedFrom":subQ1}),1.0]])]});}
            var Q4;
            {var subQ0=sQuery(id+"F5.wireOp",EDGE,"E33");var subQ1=sQuery(id+"F5.wireOp",EDGE,"E13");var subQ2=makeQuery(id+"F5.imprint","INTERSECT",VERTEX,{"disambiguationData":[OD(0.0)],"derivedFrom":[subQ1,subQ0]});Q4=makeQuery(id+"F5.imprint","IMPRINT",FACE,{"disambiguationData":[TD([[makeQuery(id+"F5.imprint","IMPRINT",EDGE,{"disambiguationData":[TD([[subQ2,-1.0]])],"derivedFrom":subQ1}),1.0]])]});}
            var Q5;
            {var subQ0=sQuery(id+"F5.wireOp",EDGE,"E33");var subQ1=sQuery(id+"F5.wireOp",EDGE,"E13");var subQ2=makeQuery(id+"F5.imprint","INTERSECT",VERTEX,{"disambiguationData":[OD(0.0)],"derivedFrom":[subQ1,subQ0]});Q5=makeQuery(id+"F5.imprint","IMPRINT",FACE,{"disambiguationData":[TD([[makeQuery(id+"F5.imprint","IMPRINT",EDGE,{"disambiguationData":[TD([[subQ2,-1.0]])],"derivedFrom":subQ1}),-1.0]])]});}
            var Q6;
            {var subQ0=sQuery(id+"F5.wireOp",EDGE,"E34");var subQ1=sQuery(id+"F5.wireOp",EDGE,"E13");var subQ2=makeQuery(id+"F5.imprint","INTERSECT",VERTEX,{"disambiguationData":[OD(0.0)],"derivedFrom":[subQ1,subQ0]});Q6=makeQuery(id+"F5.imprint","IMPRINT",FACE,{"disambiguationData":[TD([[makeQuery(id+"F5.imprint","IMPRINT",EDGE,{"disambiguationData":[TD([[subQ2,-1.0]])],"derivedFrom":subQ1}),1.0]])]});}
            var Q7;
            {var subQ0=sQuery(id+"F5.wireOp",EDGE,"E34");var subQ1=sQuery(id+"F5.wireOp",EDGE,"E13");var subQ2=makeQuery(id+"F5.imprint","INTERSECT",VERTEX,{"disambiguationData":[OD(0.0)],"derivedFrom":[subQ1,subQ0]});Q7=makeQuery(id+"F5.imprint","IMPRINT",FACE,{"disambiguationData":[TD([[makeQuery(id+"F5.imprint","IMPRINT",EDGE,{"disambiguationData":[TD([[subQ2,-1.0]])],"derivedFrom":subQ1}),-1.0]])]});}
            var Q8;
            {var subQ1=sQuery(id+"F5.wireOp",EDGE,"E36.bottom");Q8=makeQuery(id+"F5.imprint","IMPRINT",FACE,{"disambiguationData":[TD([[makeQuery(id+"F5.imprint","IMPRINT",EDGE,{"derivedFrom":subQ1}),-1.0]])]});}
            var Q9;
            {var subQ0=sQuery(id+"F5.wireOp",EDGE,"E36.top");var subQ1=sQuery(id+"F5.wireOp",EDGE,"E13");var subQ2=makeQuery(id+"F5.imprint","INTERSECT",VERTEX,{"derivedFrom":[subQ1,subQ0]});Q9=makeQuery(id+"F5.imprint","IMPRINT",FACE,{"disambiguationData":[TD([[makeQuery(id+"F5.imprint","IMPRINT",EDGE,{"disambiguationData":[TD([[subQ2,-1.0]])],"derivedFrom":subQ1}),1.0]])]});}
            var Q10;
            {var subQ0=sQuery(id+"F5.wireOp",EDGE,"E35");var subQ1=sQuery(id+"F5.wireOp",EDGE,"E13");var subQ2=makeQuery(id+"F5.imprint","INTERSECT",VERTEX,{"disambiguationData":[OD(0.0)],"derivedFrom":[subQ1,subQ0]});Q10=makeQuery(id+"F5.imprint","IMPRINT",FACE,{"disambiguationData":[TD([[makeQuery(id+"F5.imprint","IMPRINT",EDGE,{"disambiguationData":[TD([[subQ2,-1.0]])],"derivedFrom":subQ1}),-1.0]])]});}
            var Q11;
            {var subQ0=sQuery(id+"F5.wireOp",EDGE,"E35");var subQ1=sQuery(id+"F5.wireOp",EDGE,"E13");var subQ2=makeQuery(id+"F5.imprint","INTERSECT",VERTEX,{"disambiguationData":[OD(0.0)],"derivedFrom":[subQ1,subQ0]});Q11=makeQuery(id+"F5.imprint","IMPRINT",FACE,{"disambiguationData":[TD([[makeQuery(id+"F5.imprint","IMPRINT",EDGE,{"disambiguationData":[TD([[subQ2,-1.0]])],"derivedFrom":subQ1}),1.0]])]});}
            extrude(context, id + "F9", {"entities" : qUnion([Q0, Q1, Q2, Q3, Q4, Q5, Q6, Q7, Q8, Q9, Q10, Q11]), "operationType" : NewBodyOperationType.ADD, "depth" : 8 * mm, "offsetDistance" : 25 * mm});
        }
        {
            var Q0;
            Q0=makeQuery(id+"F9.opExtrude","CAP_EDGE",EDGE,{"disambiguationData":[OSD([sQuery(id+"F5.wireOp",EDGE,"E35")])],"isStart":false});
            var Q1;
            Q1=makeQuery(id+"F9.opExtrude","CAP_FACE",FACE,{"disambiguationData":[OSD([sQuery(id+"F5.wireOp",EDGE,"E31")])],"isStart":false});
            var Q2;
            Q2=makeQuery(id+"F9.opExtrude","CAP_FACE",FACE,{"disambiguationData":[OSD([sQuery(id+"F5.wireOp",EDGE,"E32")])],"isStart":false});
            var Q3;
            Q3=makeQuery(id+"F9.opExtrude","CAP_FACE",FACE,{"disambiguationData":[OSD([sQuery(id+"F5.wireOp",EDGE,"E33")])],"isStart":false});
            var Q4;
            Q4=makeQuery(id+"F9.opExtrude","CAP_FACE",FACE,{"disambiguationData":[OSD([sQuery(id+"F5.wireOp",EDGE,"E34")])],"isStart":false});
            var Q5;
            Q5=makeQuery(id+"F9.opExtrude","CAP_EDGE",EDGE,{"disambiguationData":[OSD([sQuery(id+"F5.wireOp",EDGE,"E36.left")])],"isStart":false});
            var Q6;
            Q6=makeQuery(id+"F9.opExtrude","CAP_EDGE",EDGE,{"disambiguationData":[OSD([sQuery(id+"F5.wireOp",EDGE,"E36.right")])],"isStart":false});
            var Q7;
            Q7=makeQuery(id+"F9.opExtrude","CAP_EDGE",EDGE,{"disambiguationData":[OSD([sQuery(id+"F5.wireOp",EDGE,"E36.bottom")])],"isStart":false});
            var Q8;
            Q8=makeQuery(id+"F9.opExtrude","CAP_EDGE",EDGE,{"disambiguationData":[OSD([sQuery(id+"F5.wireOp",EDGE,"E36.top")])],"isStart":false});
            fillet(context, id + "F10", {"entities" : qUnion([Q0, Q1, Q2, Q3, Q4, Q5, Q6, Q7, Q8]), "radius" : .45 * mm, "tangentPropagation" : true, "allowEdgeOverflow" : false});
        }
        {
            var Q0;
            {var subQ0=sQuery(id+"F5.wireOp",EDGE,"E35");var subQ1=sQuery(id+"F5.wireOp",EDGE,"E13");var subQ2=makeQuery(id+"F5.imprint","INTERSECT",VERTEX,{"disambiguationData":[OD(0.0)],"derivedFrom":[subQ1,subQ0]});Q0=makeQuery(id+"F5.imprint","IMPRINT",FACE,{"disambiguationData":[TD([[makeQuery(id+"F5.imprint","IMPRINT",EDGE,{"disambiguationData":[TD([[subQ2,-1.0]])],"derivedFrom":subQ1}),-1.0]])]});}
            var Q1;
            {var subQ0=sQuery(id+"F5.wireOp",EDGE,"E35");var subQ1=sQuery(id+"F5.wireOp",EDGE,"E13");var subQ2=makeQuery(id+"F5.imprint","INTERSECT",VERTEX,{"disambiguationData":[OD(0.0)],"derivedFrom":[subQ1,subQ0]});Q1=makeQuery(id+"F5.imprint","IMPRINT",FACE,{"disambiguationData":[TD([[makeQuery(id+"F5.imprint","IMPRINT",EDGE,{"disambiguationData":[TD([[subQ2,-1.0]])],"derivedFrom":subQ1}),1.0]])]});}
            var Q2;
            {var subQ1=sQuery(id+"F5.wireOp",EDGE,"E36.bottom");Q2=makeQuery(id+"F5.imprint","IMPRINT",FACE,{"disambiguationData":[TD([[makeQuery(id+"F5.imprint","IMPRINT",EDGE,{"derivedFrom":subQ1}),-1.0]])]});}
            var Q3;
            {var subQ0=sQuery(id+"F5.wireOp",EDGE,"E36.top");var subQ1=sQuery(id+"F5.wireOp",EDGE,"E13");var subQ2=makeQuery(id+"F5.imprint","INTERSECT",VERTEX,{"derivedFrom":[subQ1,subQ0]});Q3=makeQuery(id+"F5.imprint","IMPRINT",FACE,{"disambiguationData":[TD([[makeQuery(id+"F5.imprint","IMPRINT",EDGE,{"disambiguationData":[TD([[subQ2,-1.0]])],"derivedFrom":subQ1}),1.0]])]});}
            var Q4;
            {var subQ0=sQuery(id+"F5.wireOp",EDGE,"E34");var subQ1=sQuery(id+"F5.wireOp",EDGE,"E13");var subQ2=makeQuery(id+"F5.imprint","INTERSECT",VERTEX,{"disambiguationData":[OD(0.0)],"derivedFrom":[subQ1,subQ0]});Q4=makeQuery(id+"F5.imprint","IMPRINT",FACE,{"disambiguationData":[TD([[makeQuery(id+"F5.imprint","IMPRINT",EDGE,{"disambiguationData":[TD([[subQ2,-1.0]])],"derivedFrom":subQ1}),1.0]])]});}
            var Q5;
            {var subQ0=sQuery(id+"F5.wireOp",EDGE,"E34");var subQ1=sQuery(id+"F5.wireOp",EDGE,"E13");var subQ2=makeQuery(id+"F5.imprint","INTERSECT",VERTEX,{"disambiguationData":[OD(0.0)],"derivedFrom":[subQ1,subQ0]});Q5=makeQuery(id+"F5.imprint","IMPRINT",FACE,{"disambiguationData":[TD([[makeQuery(id+"F5.imprint","IMPRINT",EDGE,{"disambiguationData":[TD([[subQ2,-1.0]])],"derivedFrom":subQ1}),-1.0]])]});}
            var Q6;
            {var subQ0=sQuery(id+"F5.wireOp",EDGE,"E33");var subQ1=sQuery(id+"F5.wireOp",EDGE,"E13");var subQ2=makeQuery(id+"F5.imprint","INTERSECT",VERTEX,{"disambiguationData":[OD(0.0)],"derivedFrom":[subQ1,subQ0]});Q6=makeQuery(id+"F5.imprint","IMPRINT",FACE,{"disambiguationData":[TD([[makeQuery(id+"F5.imprint","IMPRINT",EDGE,{"disambiguationData":[TD([[subQ2,-1.0]])],"derivedFrom":subQ1}),1.0]])]});}
            var Q7;
            {var subQ0=sQuery(id+"F5.wireOp",EDGE,"E33");var subQ1=sQuery(id+"F5.wireOp",EDGE,"E13");var subQ2=makeQuery(id+"F5.imprint","INTERSECT",VERTEX,{"disambiguationData":[OD(0.0)],"derivedFrom":[subQ1,subQ0]});Q7=makeQuery(id+"F5.imprint","IMPRINT",FACE,{"disambiguationData":[TD([[makeQuery(id+"F5.imprint","IMPRINT",EDGE,{"disambiguationData":[TD([[subQ2,-1.0]])],"derivedFrom":subQ1}),-1.0]])]});}
            var Q8;
            {var subQ0=sQuery(id+"F5.wireOp",EDGE,"E32");var subQ1=sQuery(id+"F5.wireOp",EDGE,"E13");var subQ2=makeQuery(id+"F5.imprint","INTERSECT",VERTEX,{"disambiguationData":[OD(0.0)],"derivedFrom":[subQ1,subQ0]});Q8=makeQuery(id+"F5.imprint","IMPRINT",FACE,{"disambiguationData":[TD([[makeQuery(id+"F5.imprint","IMPRINT",EDGE,{"disambiguationData":[TD([[subQ2,-1.0]])],"derivedFrom":subQ1}),1.0]])]});}
            var Q9;
            {var subQ0=sQuery(id+"F5.wireOp",EDGE,"E32");var subQ1=sQuery(id+"F5.wireOp",EDGE,"E13");var subQ2=makeQuery(id+"F5.imprint","INTERSECT",VERTEX,{"disambiguationData":[OD(0.0)],"derivedFrom":[subQ1,subQ0]});Q9=makeQuery(id+"F5.imprint","IMPRINT",FACE,{"disambiguationData":[TD([[makeQuery(id+"F5.imprint","IMPRINT",EDGE,{"disambiguationData":[TD([[subQ2,-1.0]])],"derivedFrom":subQ1}),-1.0]])]});}
            var Q10;
            {var subQ0=sQuery(id+"F5.wireOp",EDGE,"E31");var subQ1=sQuery(id+"F5.wireOp",EDGE,"E13");var subQ2=makeQuery(id+"F5.imprint","INTERSECT",VERTEX,{"disambiguationData":[OD(0.0)],"derivedFrom":[subQ1,subQ0]});Q10=makeQuery(id+"F5.imprint","IMPRINT",FACE,{"disambiguationData":[TD([[makeQuery(id+"F5.imprint","IMPRINT",EDGE,{"disambiguationData":[TD([[subQ2,-1.0]])],"derivedFrom":subQ1}),-1.0]])]});}
            var Q11;
            {var subQ0=sQuery(id+"F5.wireOp",EDGE,"E31");var subQ1=sQuery(id+"F5.wireOp",EDGE,"E13");var subQ2=makeQuery(id+"F5.imprint","INTERSECT",VERTEX,{"disambiguationData":[OD(0.0)],"derivedFrom":[subQ1,subQ0]});Q11=makeQuery(id+"F5.imprint","IMPRINT",FACE,{"disambiguationData":[TD([[makeQuery(id+"F5.imprint","IMPRINT",EDGE,{"disambiguationData":[TD([[subQ2,-1.0]])],"derivedFrom":subQ1}),1.0]])]});}
            extrude(context, id + "F11", {"entities" : qUnion([Q0, Q1, Q2, Q3, Q4, Q5, Q6, Q7, Q8, Q9, Q10, Q11]), "operationType" : NewBodyOperationType.REMOVE, "depth" : 1.8 * mm, "offsetDistance" : 25 * mm});
        }
        {
            var Q0;
            Q0=qCreatedBy(makeId("Top.planeOp"),FACE);
            var sketch = newSketch(context, id + "F12", { "sketchPlane" : qUnion([Q0])});
            skCircle(sketch, "E37", {"center": v(0, 0) * mm, "radius": 13.47 * mm});
            skSolve(sketch);
        }
        {
            var Q0;
            Q0 = qSketchRegion(id + "F12", true);
            extrude(context, id + "F13", {"entities" : qUnion([Q0]), "operationType" : NewBodyOperationType.REMOVE, "depth" : 1 * mm, "offsetDistance" : 25 * mm});
        }
        {
            var Q0;
            {var subQ0=sQuery(id+"F0.wireOp",EDGE,"E8.right");var subQ1=sQuery(id+"F0.wireOp",EDGE,"E1.0");var subQ2=makeQuery(id+"F0.imprint","INTERSECT",VERTEX,{"disambiguationData":[OD(1.0)],"derivedFrom":[subQ1,subQ0]});Q0=makeQuery(id+"F0.imprint","IMPRINT",FACE,{"disambiguationData":[TD([[makeQuery(id+"F0.imprint","IMPRINT",EDGE,{"disambiguationData":[TD([[subQ2,-1.0]])],"derivedFrom":subQ1}),1.0]])]});}
            var Q1;
            {var subQ0=sQuery(id+"F0.wireOp",EDGE,"E9.right");var subQ1=sQuery(id+"F0.wireOp",EDGE,"E1.0");var subQ2=makeQuery(id+"F0.imprint","INTERSECT",VERTEX,{"disambiguationData":[OD(1.0)],"derivedFrom":[subQ1,subQ0]});Q1=makeQuery(id+"F0.imprint","IMPRINT",FACE,{"disambiguationData":[TD([[makeQuery(id+"F0.imprint","IMPRINT",EDGE,{"disambiguationData":[TD([[subQ2,-1.0]])],"derivedFrom":subQ1}),1.0]])]});}
            var Q2;
            {var subQ0=sQuery(id+"F0.wireOp",EDGE,"E3.right");var subQ1=sQuery(id+"F0.wireOp",EDGE,"E1.0");var subQ2=makeQuery(id+"F0.imprint","INTERSECT",VERTEX,{"disambiguationData":[OD(0.0)],"derivedFrom":[subQ1,subQ0]});Q2=makeQuery(id+"F0.imprint","IMPRINT",FACE,{"disambiguationData":[TD([[makeQuery(id+"F0.imprint","IMPRINT",EDGE,{"disambiguationData":[TD([[subQ2,1.0]])],"derivedFrom":subQ1}),1.0]])]});}
            var Q3;
            {var subQ0=sQuery(id+"F0.wireOp",EDGE,"E3.left");var subQ1=sQuery(id+"F0.wireOp",EDGE,"E1.0");var subQ2=makeQuery(id+"F0.imprint","INTERSECT",VERTEX,{"disambiguationData":[OD(0.0)],"derivedFrom":[subQ1,subQ0]});Q3=makeQuery(id+"F0.imprint","IMPRINT",FACE,{"disambiguationData":[TD([[makeQuery(id+"F0.imprint","IMPRINT",EDGE,{"disambiguationData":[TD([[subQ2,-1.0]])],"derivedFrom":subQ1}),1.0]])]});}
            var Q4;
            {var subQ0=sQuery(id+"F0.wireOp",EDGE,"E2.left");var subQ1=sQuery(id+"F0.wireOp",EDGE,"E1.0");var subQ2=makeQuery(id+"F0.imprint","INTERSECT",VERTEX,{"disambiguationData":[OD(0.0)],"derivedFrom":[subQ1,subQ0]});Q4=makeQuery(id+"F0.imprint","IMPRINT",FACE,{"disambiguationData":[TD([[makeQuery(id+"F0.imprint","IMPRINT",EDGE,{"disambiguationData":[TD([[subQ2,-1.0]])],"derivedFrom":subQ1}),1.0]])]});}
            var Q5;
            {var subQ0=sQuery(id+"F0.wireOp",EDGE,"E9.left");var subQ1=sQuery(id+"F0.wireOp",EDGE,"E1.0");var subQ2=makeQuery(id+"F0.imprint","INTERSECT",VERTEX,{"disambiguationData":[OD(0.0)],"derivedFrom":[subQ1,subQ0]});Q5=makeQuery(id+"F0.imprint","IMPRINT",FACE,{"disambiguationData":[TD([[makeQuery(id+"F0.imprint","IMPRINT",EDGE,{"disambiguationData":[TD([[subQ2,-1.0]])],"derivedFrom":subQ1}),1.0]])]});}
            var Q6;
            {var subQ0=sQuery(id+"F0.wireOp",EDGE,"E6.top");var subQ1=sQuery(id+"F0.wireOp",EDGE,"E1.0");var subQ2=makeQuery(id+"F0.imprint","INTERSECT",VERTEX,{"disambiguationData":[OD(0.0)],"derivedFrom":[subQ1,subQ0]});Q6=makeQuery(id+"F0.imprint","IMPRINT",FACE,{"disambiguationData":[TD([[makeQuery(id+"F0.imprint","IMPRINT",EDGE,{"disambiguationData":[TD([[subQ2,-1.0]])],"derivedFrom":subQ1}),1.0]])]});}
            var Q7;
            {var subQ0=sQuery(id+"F0.wireOp",EDGE,"E3.right");var subQ1=sQuery(id+"F0.wireOp",EDGE,"E1.0");var subQ2=makeQuery(id+"F0.imprint","INTERSECT",VERTEX,{"disambiguationData":[OD(1.0)],"derivedFrom":[subQ1,subQ0]});Q7=makeQuery(id+"F0.imprint","IMPRINT",FACE,{"disambiguationData":[TD([[makeQuery(id+"F0.imprint","IMPRINT",EDGE,{"disambiguationData":[TD([[subQ2,-1.0]])],"derivedFrom":subQ1}),1.0]])]});}
            extrude(context, id + "F14", {"entities" : qUnion([Q0, Q1, Q2, Q3, Q4, Q5, Q6, Q7]), "operationType" : NewBodyOperationType.REMOVE, "depth" : 1 * mm, "offsetDistance" : 25 * mm});
        }
        {
            var Q0;
            Q0=makeQuery(id+"F14.boolean.opBoolean","COPY",EDGE,{"derivedFrom":makeQuery(id+"F14.opExtrude","SWEPT_EDGE",EDGE,{"disambiguationData":[OSD([sQuery(id+"F0.wireOp",EDGE,"E1.0"),sQuery(id+"F0.wireOp",EDGE,"E6.top")])]})});
            var Q1;
            {var subQ0=sQuery(id+"F0.wireOp",EDGE,"E3.right");var subQ1=sQuery(id+"F0.wireOp",EDGE,"E1.0");Q1=makeQuery(id+"F14.boolean.opBoolean","COPY",EDGE,{"derivedFrom":makeQuery(id+"F14.opExtrude","SWEPT_EDGE",EDGE,{"disambiguationData":[OSD([subQ1,subQ0]),TDD([makeQuery(id+"F0.imprint","INTERSECT",VERTEX,{"disambiguationData":[OD(1.0)],"derivedFrom":[subQ1,subQ0]})])]})});}
            var Q2;
            Q2=makeQuery(id+"F14.boolean.opBoolean","COPY",EDGE,{"derivedFrom":makeQuery(id+"F14.opExtrude","SWEPT_EDGE",EDGE,{"disambiguationData":[OSD([sQuery(id+"F0.wireOp",EDGE,"E1.0"),sQuery(id+"F0.wireOp",EDGE,"E7.bottom")])]})});
            var Q3;
            {var subQ0=sQuery(id+"F0.wireOp",EDGE,"E3.left");var subQ1=sQuery(id+"F0.wireOp",EDGE,"E1.0");Q3=makeQuery(id+"F14.boolean.opBoolean","COPY",EDGE,{"derivedFrom":makeQuery(id+"F14.opExtrude","SWEPT_EDGE",EDGE,{"disambiguationData":[OSD([subQ1,subQ0]),TDD([makeQuery(id+"F0.imprint","INTERSECT",VERTEX,{"disambiguationData":[OD(1.0)],"derivedFrom":[subQ1,subQ0]})])]})});}
            var Q4;
            {var subQ0=sQuery(id+"F0.wireOp",EDGE,"E2.left");var subQ1=sQuery(id+"F0.wireOp",EDGE,"E1.0");Q4=makeQuery(id+"F14.boolean.opBoolean","COPY",EDGE,{"derivedFrom":makeQuery(id+"F14.opExtrude","SWEPT_EDGE",EDGE,{"disambiguationData":[OSD([subQ1,subQ0]),TDD([makeQuery(id+"F0.imprint","INTERSECT",VERTEX,{"disambiguationData":[OD(1.0)],"derivedFrom":[subQ1,subQ0]})])]})});}
            var Q5;
            {var subQ0=sQuery(id+"F0.wireOp",EDGE,"E8.right");var subQ1=sQuery(id+"F0.wireOp",EDGE,"E1.0");Q5=makeQuery(id+"F14.boolean.opBoolean","COPY",EDGE,{"derivedFrom":makeQuery(id+"F14.opExtrude","SWEPT_EDGE",EDGE,{"disambiguationData":[OSD([subQ1,subQ0]),TDD([makeQuery(id+"F0.imprint","INTERSECT",VERTEX,{"disambiguationData":[OD(1.0)],"derivedFrom":[subQ1,subQ0]})])]})});}
            var Q6;
            Q6=makeQuery(id+"F14.boolean.opBoolean","COPY",EDGE,{"derivedFrom":makeQuery(id+"F14.opExtrude","SWEPT_EDGE",EDGE,{"disambiguationData":[OSD([sQuery(id+"F0.wireOp",EDGE,"E1.0"),sQuery(id+"F0.wireOp",EDGE,"E9.right")])]})});
            var Q7;
            {var subQ0=sQuery(id+"F0.wireOp",EDGE,"E9.left");var subQ1=sQuery(id+"F0.wireOp",EDGE,"E1.0");Q7=makeQuery(id+"F14.boolean.opBoolean","COPY",EDGE,{"derivedFrom":makeQuery(id+"F14.opExtrude","SWEPT_EDGE",EDGE,{"disambiguationData":[OSD([subQ1,subQ0]),TDD([makeQuery(id+"F0.imprint","INTERSECT",VERTEX,{"disambiguationData":[OD(1.0)],"derivedFrom":[subQ1,subQ0]})])]})});}
            var Q8;
            Q8=makeQuery(id+"F14.boolean.opBoolean","COPY",EDGE,{"derivedFrom":makeQuery(id+"F14.opExtrude","SWEPT_EDGE",EDGE,{"disambiguationData":[OSD([sQuery(id+"F0.wireOp",EDGE,"E1.0"),sQuery(id+"F0.wireOp",EDGE,"E6.bottom")])]})});
            var Q9;
            {var subQ0=sQuery(id+"F0.wireOp",EDGE,"E3.left");var subQ1=sQuery(id+"F0.wireOp",EDGE,"E1.0");Q9=makeQuery(id+"F14.boolean.opBoolean","COPY",EDGE,{"derivedFrom":makeQuery(id+"F14.opExtrude","SWEPT_EDGE",EDGE,{"disambiguationData":[OSD([subQ1,subQ0]),TDD([makeQuery(id+"F0.imprint","INTERSECT",VERTEX,{"disambiguationData":[OD(0.0)],"derivedFrom":[subQ1,subQ0]})])]})});}
            var Q10;
            {var subQ0=sQuery(id+"F0.wireOp",EDGE,"E3.right");var subQ1=sQuery(id+"F0.wireOp",EDGE,"E1.0");Q10=makeQuery(id+"F14.boolean.opBoolean","COPY",EDGE,{"derivedFrom":makeQuery(id+"F14.opExtrude","SWEPT_EDGE",EDGE,{"disambiguationData":[OSD([subQ1,subQ0]),TDD([makeQuery(id+"F0.imprint","INTERSECT",VERTEX,{"disambiguationData":[OD(0.0)],"derivedFrom":[subQ1,subQ0]})])]})});}
            var Q11;
            {var subQ0=sQuery(id+"F0.wireOp",EDGE,"E2.left");var subQ1=sQuery(id+"F0.wireOp",EDGE,"E1.0");Q11=makeQuery(id+"F14.boolean.opBoolean","COPY",EDGE,{"derivedFrom":makeQuery(id+"F14.opExtrude","SWEPT_EDGE",EDGE,{"disambiguationData":[OSD([subQ1,subQ0]),TDD([makeQuery(id+"F0.imprint","INTERSECT",VERTEX,{"disambiguationData":[OD(0.0)],"derivedFrom":[subQ1,subQ0]})])]})});}
            var Q12;
            {var subQ0=sQuery(id+"F0.wireOp",EDGE,"E8.right");var subQ1=sQuery(id+"F0.wireOp",EDGE,"E1.0");Q12=makeQuery(id+"F14.boolean.opBoolean","COPY",EDGE,{"derivedFrom":makeQuery(id+"F14.opExtrude","SWEPT_EDGE",EDGE,{"disambiguationData":[OSD([subQ1,subQ0]),TDD([makeQuery(id+"F0.imprint","INTERSECT",VERTEX,{"disambiguationData":[OD(0.0)],"derivedFrom":[subQ1,subQ0]})])]})});}
            var Q13;
            {var subQ0=sQuery(id+"F0.wireOp",EDGE,"E9.left");var subQ1=sQuery(id+"F0.wireOp",EDGE,"E1.0");Q13=makeQuery(id+"F14.boolean.opBoolean","COPY",EDGE,{"derivedFrom":makeQuery(id+"F14.opExtrude","SWEPT_EDGE",EDGE,{"disambiguationData":[OSD([subQ1,subQ0]),TDD([makeQuery(id+"F0.imprint","INTERSECT",VERTEX,{"disambiguationData":[OD(0.0)],"derivedFrom":[subQ1,subQ0]})])]})});}
            var Q14;
            Q14=makeQuery(id+"F14.boolean.opBoolean","COPY",EDGE,{"derivedFrom":makeQuery(id+"F14.opExtrude","SWEPT_EDGE",EDGE,{"disambiguationData":[OSD([sQuery(id+"F0.wireOp",EDGE,"E1.0"),sQuery(id+"F0.wireOp",EDGE,"E2.right")])]})});
            var Q15;
            Q15=makeQuery(id+"F14.boolean.opBoolean","COPY",EDGE,{"derivedFrom":makeQuery(id+"F14.opExtrude","SWEPT_EDGE",EDGE,{"disambiguationData":[OSD([sQuery(id+"F0.wireOp",EDGE,"E1.0"),sQuery(id+"F0.wireOp",EDGE,"E7.top")])]})});
            fillet(context, id + "F15", {"entities" : qUnion([Q0, Q1, Q2, Q3, Q4, Q5, Q6, Q7, Q8, Q9, Q10, Q11, Q12, Q13, Q14, Q15]), "radius" : 1 * mm, "tangentPropagation" : true, "allowEdgeOverflow" : false});
        }
    });
